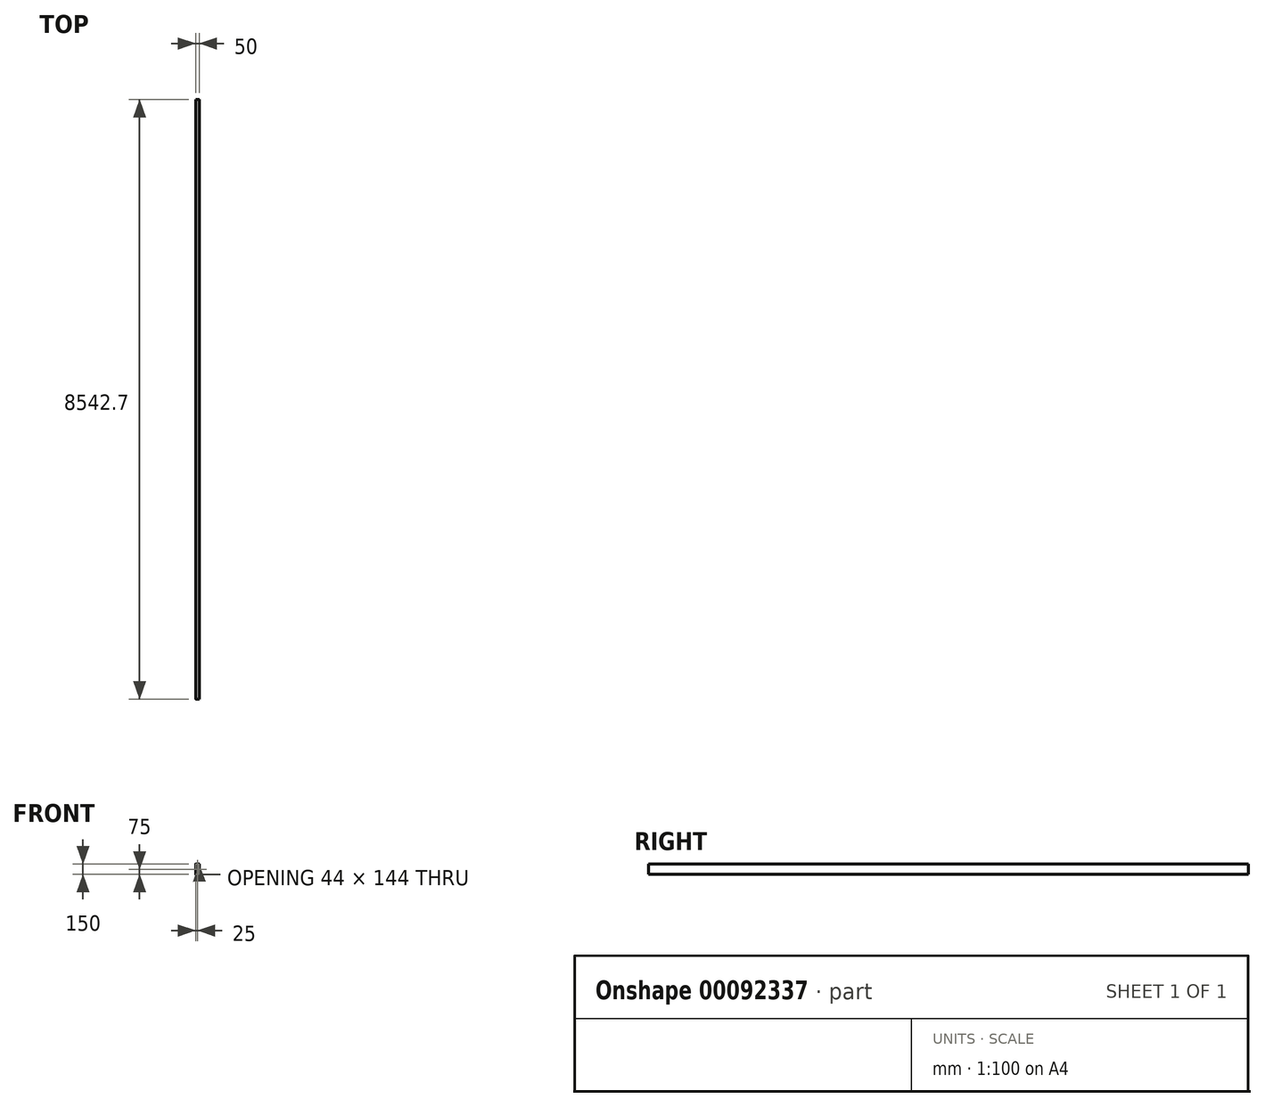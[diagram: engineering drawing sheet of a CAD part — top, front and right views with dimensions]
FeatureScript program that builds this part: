
annotation { "Feature Type Name" : "Feature", "Feature Type Description" : "" }
export const myFeature = defineFeature(function(context is Context, id is Id, definition is map)
    precondition{}
    {
        {
            var Q0;
            Q0=qCreatedBy(makeId("Front.planeOp"),FACE);
            var sketch = newSketch(context, id + "F0", { "sketchPlane" : qUnion([Q0])});
            skLineSegment(sketch, "E0.bottom", {"start": v(2.4, 0) * mm, "end": v(47.6, 0) * mm});
            skLineSegment(sketch, "E0.top", {"start": v(2.4, 150) * mm, "end": v(47.6, 150) * mm});
            skLineSegment(sketch, "E0.left", {"start": v(0, 2.4) * mm, "end": v(0, 147.6) * mm});
            skLineSegment(sketch, "E0.right", {"start": v(50, 2.4) * mm, "end": v(50, 147.6) * mm});
            skPoint(sketch, "E1.visualSharp", {"position": v(0, 150) * mm});
            skArc(sketch, "E1.filletArc", {"start": v(2.4, 150) * mm, "mid": v(0.7, 149.3) * mm, "end": v(0, 147.6) * mm});
            skPoint(sketch, "E2.visualSharp", {"position": v(50, 150) * mm});
            skArc(sketch, "E2.filletArc", {"start": v(50, 147.6) * mm, "mid": v(49.3, 149.3) * mm, "end": v(47.6, 150) * mm});
            skPoint(sketch, "E3.visualSharp", {"position": v(0, 0) * mm});
            skArc(sketch, "E3.filletArc", {"start": v(0, 2.4) * mm, "mid": v(0.7, 0.7) * mm, "end": v(2.4, 0) * mm});
            skPoint(sketch, "E4.visualSharp", {"position": v(50, 0) * mm});
            skArc(sketch, "E4.filletArc", {"start": v(47.6, 0) * mm, "mid": v(49.3, 0.7) * mm, "end": v(50, 2.4) * mm});
            skLineSegment(sketch, "E5.0", {"start": v(3, 5.4) * mm, "end": v(3, 144.6) * mm});
            skLineSegment(sketch, "E6.0", {"start": v(5.4, 147) * mm, "end": v(44.6, 147) * mm});
            skLineSegment(sketch, "E7.0", {"start": v(47, 5.4) * mm, "end": v(47, 144.6) * mm});
            skLineSegment(sketch, "E8.0", {"start": v(5.4, 3) * mm, "end": v(44.6, 3) * mm});
            skArc(sketch, "E9.filletArc", {"start": v(5.4, 147) * mm, "mid": v(3.7, 146.3) * mm, "end": v(3, 144.6) * mm});
            skArc(sketch, "E10.filletArc", {"start": v(3, 5.4) * mm, "mid": v(3.7, 3.7) * mm, "end": v(5.4, 3) * mm});
            skArc(sketch, "E11.filletArc", {"start": v(47, 144.6) * mm, "mid": v(46.3, 146.3) * mm, "end": v(44.6, 147) * mm});
            skArc(sketch, "E12.filletArc", {"start": v(44.6, 3) * mm, "mid": v(46.3, 3.7) * mm, "end": v(47, 5.4) * mm});
            skSolve(sketch);
        }
        {
            var Q0;
            Q0=qSketchRegion(id+"F0",true);
            extrude(context, id + "F1", {"entities" : qUnion([Q0]), "depth" : 8542.7 * mm, "offsetDistance" : 25 * mm});
        }
    });
